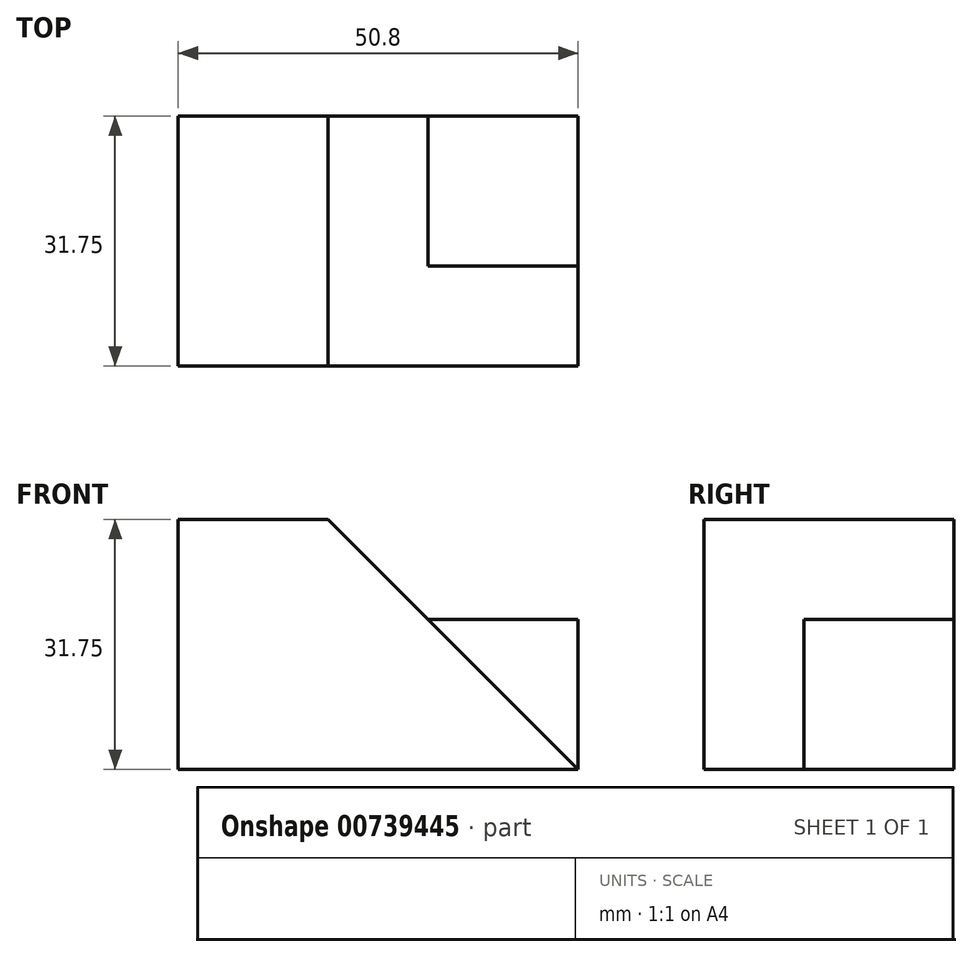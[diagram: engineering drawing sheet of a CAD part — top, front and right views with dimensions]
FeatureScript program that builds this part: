
annotation { "Feature Type Name" : "Feature", "Feature Type Description" : "" }
export const myFeature = defineFeature(function(context is Context, id is Id, definition is map)
    precondition{}
    {
        {
            var Q0;
            Q0=qCreatedBy(makeId("Front.planeOp"),FACE);
            var sketch = newSketch(context, id + "F0", { "sketchPlane" : qUnion([Q0])});
            skLineSegment(sketch, "E0.bottom", {"start": v(0, 0) * mm, "end": v(50.8, 0) * mm});
            skLineSegment(sketch, "E0.top", {"start": v(0, 31.75) * mm, "end": v(50.8, 31.75) * mm});
            skLineSegment(sketch, "E0.left", {"start": v(0, 0) * mm, "end": v(0, 31.75) * mm});
            skLineSegment(sketch, "E0.right", {"start": v(50.8, 0) * mm, "end": v(50.8, 31.75) * mm});
            skSolve(sketch);
        }
        {
            var Q0;
            Q0=makeQuery(id+"F0.imprint","IMPRINT",FACE,{"disambiguationData":[TD([[makeQuery(id+"F0.imprint","IMPRINT",EDGE,{"derivedFrom":sQuery(id+"F0.wireOp",EDGE,"E0.bottom")}),1.0]])]});
            extrude(context, id + "F1", {"entities" : qUnion([Q0]), "depth" : 31.75 * mm, "offsetDistance" : 25.4 * mm});
        }
        {
            var Q0;
            Q0=makeQuery(id+"F1.opExtrude","CAP_FACE",FACE,{"disambiguationData":[OSD([sQuery(id+"F0.wireOp",EDGE,"E0.bottom"),sQuery(id+"F0.wireOp",EDGE,"E0.top"),sQuery(id+"F0.wireOp",EDGE,"E0.left"),sQuery(id+"F0.wireOp",EDGE,"E0.right")])],"isStart":true});
            var sketch = newSketch(context, id + "F2", { "sketchPlane" : qUnion([Q0])});
            skLineSegment(sketch, "E1", {"start": v(-19.05, 31.75) * mm, "end": v(-31.75, 19.05) * mm});
            skLineSegment(sketch, "E2", {"start": v(-31.75, 19.05) * mm, "end": v(-50.8, 19.05) * mm});
            skLineSegment(sketch, "E3", {"start": v(-50.8, 19.05) * mm, "end": v(-50.8, 31.75) * mm});
            skLineSegment(sketch, "E4", {"start": v(-50.8, 31.75) * mm, "end": v(-19.05, 31.75) * mm});
            skSolve(sketch);
        }
        {
            var Q0;
            Q0=makeQuery(id+"F2.imprint","IMPRINT",FACE,{"disambiguationData":[TD([[makeQuery(id+"F2.imprint","IMPRINT",EDGE,{"derivedFrom":sQuery(id+"F2.wireOp",EDGE,"E1")}),-1.0]])]});
            extrude(context, id + "F3", {"entities" : qUnion([Q0]), "operationType" : NewBodyOperationType.REMOVE, "oppositeDirection" : true, "depth" : 19.05 * mm, "offsetDistance" : 25.4 * mm});
        }
        {
            var Q0;
            Q0=makeQuery(id+"F1.opExtrude","CAP_FACE",FACE,{"disambiguationData":[OSD([sQuery(id+"F0.wireOp",EDGE,"E0.bottom"),sQuery(id+"F0.wireOp",EDGE,"E0.top"),sQuery(id+"F0.wireOp",EDGE,"E0.left"),sQuery(id+"F0.wireOp",EDGE,"E0.right")])],"isStart":false});
            var sketch = newSketch(context, id + "F4", { "sketchPlane" : qUnion([Q0])});
            skLineSegment(sketch, "E5", {"start": v(19.05, 31.75) * mm, "end": v(50.8, 0) * mm});
            skLineSegment(sketch, "E6", {"start": v(50.8, 0) * mm, "end": v(50.8, 31.75) * mm});
            skLineSegment(sketch, "E7", {"start": v(50.8, 31.75) * mm, "end": v(19.05, 31.75) * mm});
            skSolve(sketch);
        }
        {
            var Q0;
            Q0=makeQuery(id+"F4.imprint","IMPRINT",FACE,{"disambiguationData":[TD([[makeQuery(id+"F4.imprint","IMPRINT",EDGE,{"derivedFrom":sQuery(id+"F4.wireOp",EDGE,"E5")}),1.0]])]});
            extrude(context, id + "F5", {"entities" : qUnion([Q0]), "operationType" : NewBodyOperationType.REMOVE, "oppositeDirection" : true, "depth" : 12.7 * mm, "offsetDistance" : 25.4 * mm});
        }
    });
